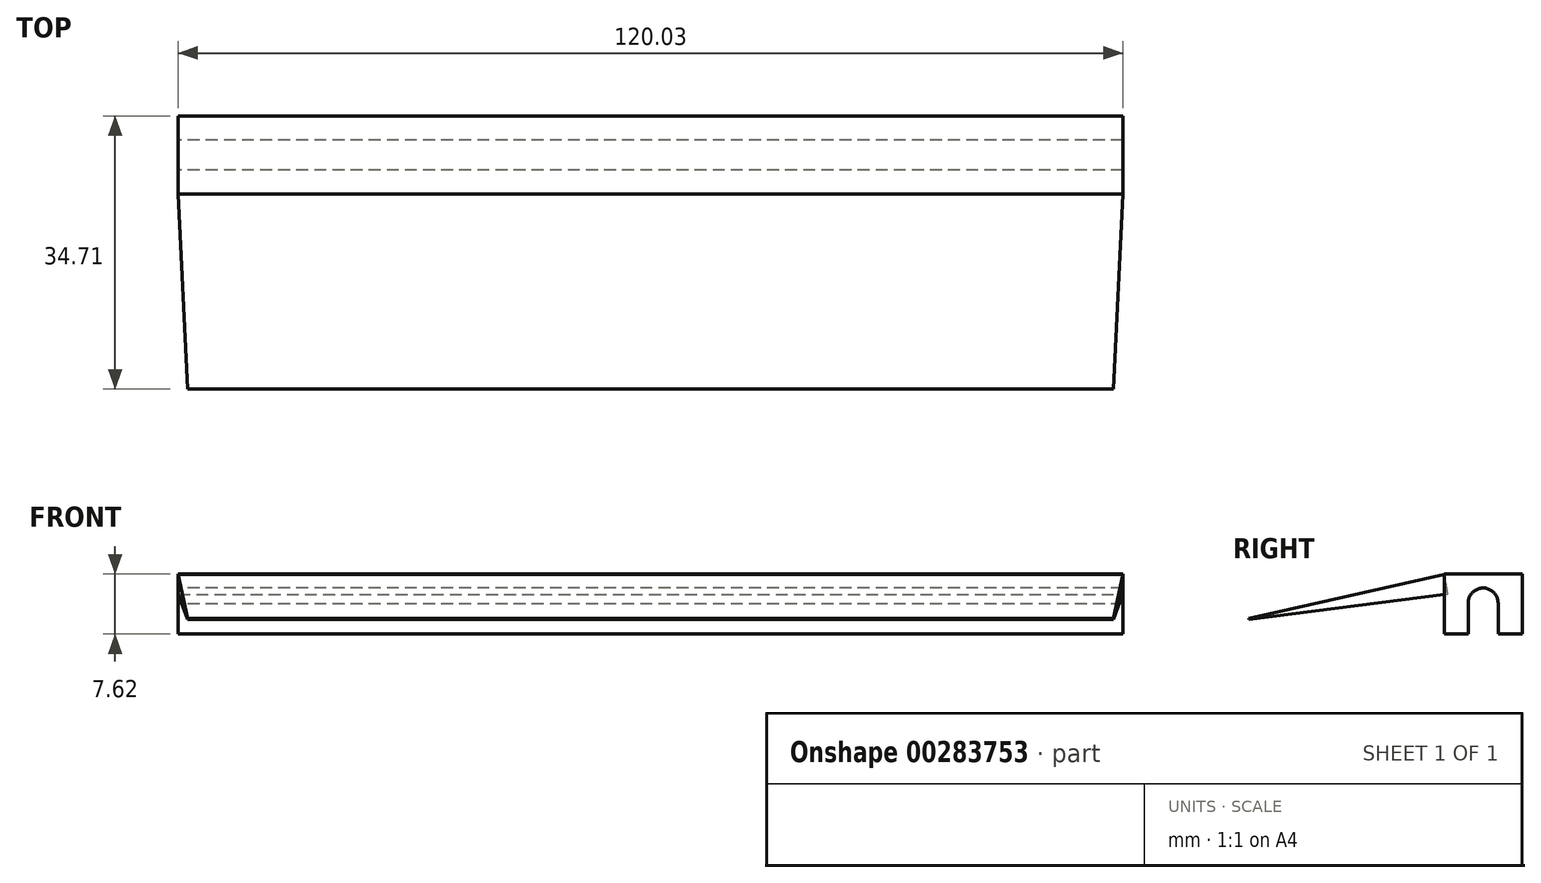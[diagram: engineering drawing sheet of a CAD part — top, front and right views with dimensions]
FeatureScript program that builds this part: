
annotation { "Feature Type Name" : "Feature", "Feature Type Description" : "" }
export const myFeature = defineFeature(function(context is Context, id is Id, definition is map)
    precondition{}
    {
        {
            var Q0;
            Q0=qCreatedBy(makeId("Right.planeOp"),FACE);
            var sketch = newSketch(context, id + "F0", { "sketchPlane" : qUnion([Q0])});
            skLineSegment(sketch, "E0", {"start": v(0, 0) * mm, "end": v(0, 7.62) * mm});
            skLineSegment(sketch, "E1", {"start": v(0, 7.62) * mm, "end": v(9.9, 7.62) * mm});
            skLineSegment(sketch, "E2", {"start": v(9.9, 7.62) * mm, "end": v(9.9, 0) * mm});
            skLineSegment(sketch, "E3", {"start": v(9.9, 0) * mm, "end": v(6.86, 0) * mm});
            skLineSegment(sketch, "E4", {"start": v(6.86, 0) * mm, "end": v(6.86, 3.83) * mm});
            skLineSegment(sketch, "E5", {"start": v(0, 0) * mm, "end": v(3.05, 0) * mm});
            skLineSegment(sketch, "E6", {"start": v(3.05, 0) * mm, "end": v(3.05, 3.83) * mm});
            skArc(sketch, "E7", {"start": v(6.86, 3.83) * mm, "mid": v(4.95, 5.84) * mm, "end": v(3.05, 3.83) * mm});
            skSolve(sketch);
        }
        {
            var Q0;
            Q0=makeQuery(id+"F0.imprint","IMPRINT",FACE,{"disambiguationData":[TD([[makeQuery(id+"F0.imprint","IMPRINT",EDGE,{"derivedFrom":sQuery(id+"F0.wireOp",EDGE,"E0")}),-1.0]])]});
            extrude(context, id + "F1", {"entities" : qUnion([Q0]), "endBound" : BoundingType.SYMMETRIC, "depth" : 120 * mm});
        }
        {
            var Q0;
            Q0=qCreatedBy(makeId("Front.planeOp"),FACE);
            var Q1;
            Q1=makeQuery(id+"F1.opExtrude","SWEPT_EDGE",EDGE,{"disambiguationData":[OSD([sQuery(id+"F0.wireOp",EDGE,"E0"),sQuery(id+"F0.wireOp",EDGE,"E1")])]});
            cPlane(context, id + "F2", {"entities" : qUnion([Q0, Q1]), "cplaneType" : CPlaneType.LINE_ANGLE, "offset" : 25.4 * mm, "angle" : 10 * degree, "oppositeDirection" : true, "width" : 152.4 * mm, "height" : 152.4 * mm});
        }
        {
            var Q0;
            Q0=qCreatedBy(id+"F2.planeOp",FACE);
            var sketch = newSketch(context, id + "F3", { "sketchPlane" : qUnion([Q0])});
            skLineSegment(sketch, "E8", {"start": v(60.03, 7.48) * mm, "end": v(60.03, 4.93) * mm});
            skLineSegment(sketch, "E9", {"start": v(60.03, 4.93) * mm, "end": v(-59.97, 4.93) * mm});
            skLineSegment(sketch, "E10", {"start": v(-59.97, 4.93) * mm, "end": v(-59.97, 7.48) * mm});
            skLineSegment(sketch, "E11", {"start": v(-59.97, 7.48) * mm, "end": v(60.03, 7.48) * mm});
            skSolve(sketch);
        }
        {
            var Q0;
            Q0 = qSketchRegion(id + "F3", true);
            extrude(context, id + "F4", {"entities" : qUnion([Q0]), "operationType" : NewBodyOperationType.ADD, "oppositeDirection" : true, "depth" : 25.4 * mm, "hasDraft" : true, "draftAngle" : 2.7 * degree, "draftPullDirection" : true});
        }
    });
